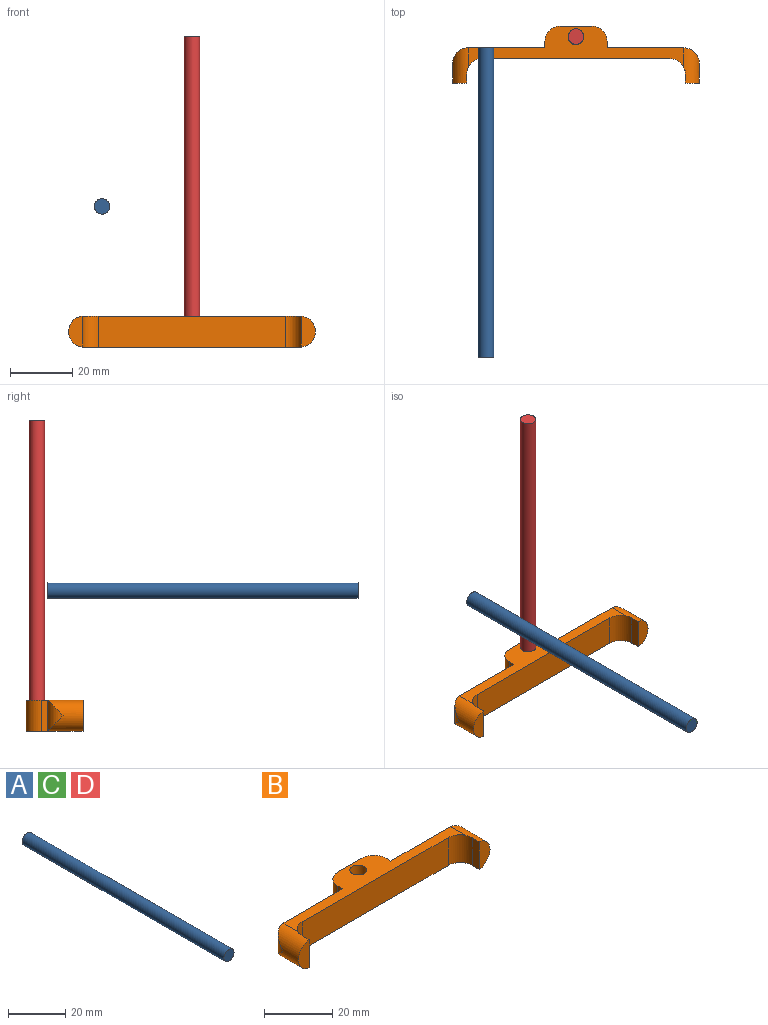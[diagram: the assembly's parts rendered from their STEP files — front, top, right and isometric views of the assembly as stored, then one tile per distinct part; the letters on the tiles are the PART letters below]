
ASSEMBLY  parts=4 mates=1
PART A: 3 faces, bbox 5x100x5 mm
  f0: cylinder r=2.5mm len=100mm, axis (0,1,0), area 1570.8mm2, adj f1,f2
  f1: plane 5x5mm, normal (0,-1,0), area 19.6mm2, adj f0
  f2: plane 5x5mm, normal (0,1,0), area 19.6mm2, adj f0
PART B: 21 faces, bbox 79.6x18.4x10 mm
  f0: plane 24.78x10mm, normal (0,1,0), area 247.7mm2, adj f2,f3,f12,f14
  f1: plane 60.55x10mm, normal (0,-1,0), area 605.5mm2, adj f2,f3,f19,f20
  f2: plane 69.55x13.32mm, normal (0,0,1), area 360.3mm2, adj f0,f1,f4,f9,f11,f13,f14,f15
  f3: plane 69.55x13.32mm, normal (0,0,-1), area 360.3mm2, adj f0,f1,f4,f9,f11,f13,f14,f15
  f4: plane 24.78x10mm, normal (0,1,0), area 247.7mm2, adj f2,f3,f10,f13
  f5: plane 9.95x2.9mm, normal (1,0,0), area 28.9mm2, adj f6,f9,f20
  f6: plane 9.95x4.5mm, normal (0,-1,0), area 34.3mm2, adj f5,f9
  f7: plane 9.95x2.9mm, normal (-1,0,0), area 28.9mm2, adj f8,f11,f19
  f8: plane 9.95x4.5mm, normal (0,-1,0), area 34.3mm2, adj f7,f11
  f9: cylinder r=5mm len=11.4mm, axis (0,-1,0), area 146.2mm2, adj f2,f3,f5,f6,f10,f20
  f10: cylinder r=5mm len=10mm, axis (0,0,-1), area 50mm2, adj f4,f9
  f11: cylinder r=5mm len=11.4mm, axis (0,1,0), area 146.2mm2, adj f2,f3,f7,f8,f12,f19
  f12: cylinder r=5mm len=10mm, axis (0,0,1), area 50mm2, adj f0,f11
  f13: plane 10x2mm, normal (-1,0,0), area 20mm2, adj f2,f3,f4,f18
  f14: plane 10x2mm, normal (1,0,0), area 20mm2, adj f0,f2,f3,f17
  f15: plane 10x10mm, normal (0,1,0), area 100mm2, adj f2,f3,f17,f18
  f16: cylinder r=2.5mm len=10mm, axis (0,0,1), area 157.1mm2, adj f2,f3
  f17: cylinder r=5mm len=10mm, axis (0,0,1), area 78.5mm2, adj f2,f3,f14,f15
  f18: cylinder r=5mm len=10mm, axis (0,0,-1), area 78.5mm2, adj f2,f3,f13,f15
  f19: cylinder r=5mm len=10mm, axis (0,0,-1), area 78.5mm2, adj f1,f2,f3,f7,f11
  f20: cylinder r=5mm len=10mm, axis (0,0,1), area 78.5mm2, adj f1,f2,f3,f5,f9
PART C: same geometry as A
PART D: same geometry as A
PLACE A t=(13.61,-14.24,-74.72)mm
PLACE B t=(13.61,-14.24,-74.72)mm
PLACE C t=(13.61,-14.24,-74.72)mm
PLACE D rot(axis=(1,0,0),90deg) t=(42.59,29.57,20.24)mm
MATE cylindrical D.f0 <-> B.f16  axis (0,0,-1) through (6.55,-10.74,-79.76)mm
